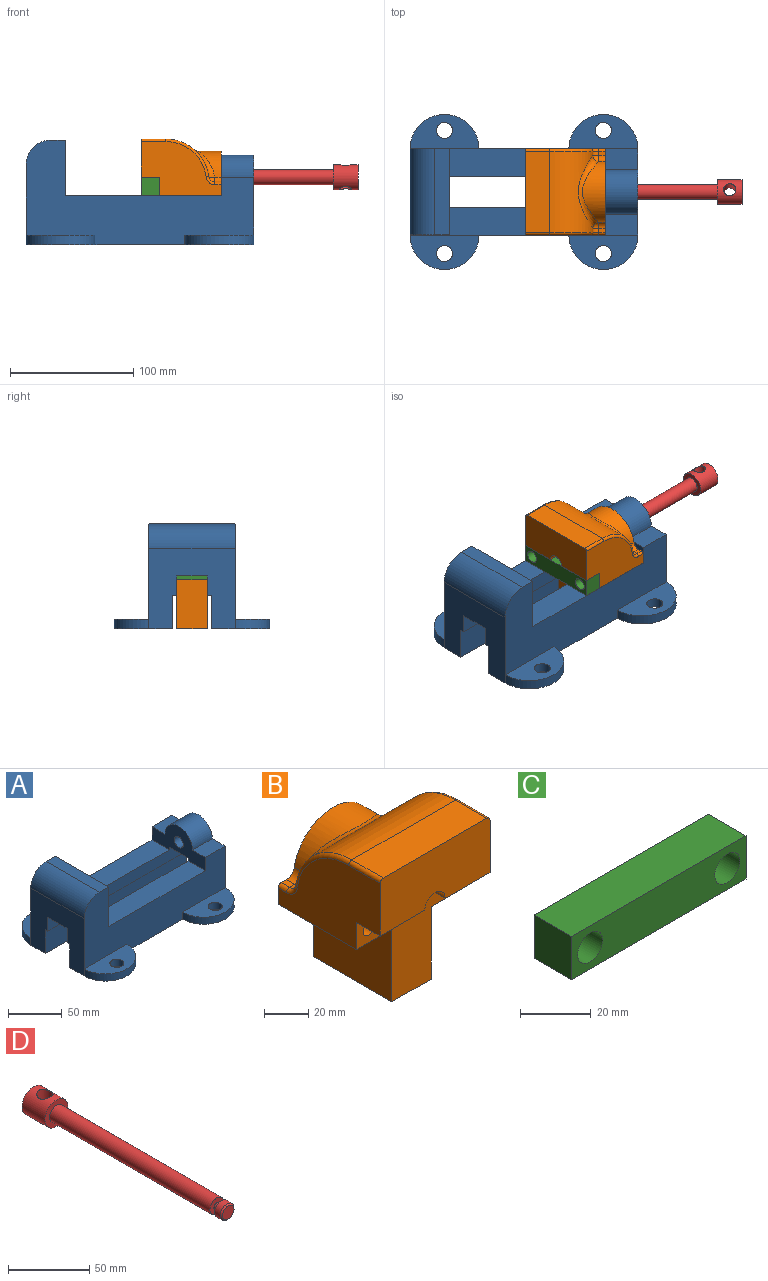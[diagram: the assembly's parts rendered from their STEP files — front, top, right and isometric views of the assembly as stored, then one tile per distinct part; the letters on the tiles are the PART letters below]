
ASSEMBLY  parts=4 mates=5
PART A: 36 faces, bbox 185x126x85 mm
  f0: plane 185x85mm, normal (0,1,0), area 8248.2mm2, adj f2,f3,f5,f6,f7,f8,f9,f10
  f1: plane 185x47mm, normal (0,0,-1), area 5712.5mm2, adj f2,f3,f11,f15,f30,f32,f33,f35
  f2: plane 73x70mm, normal (1,0,0), area 2981.8mm2, adj f0,f1,f9,f11,f12,f13,f14,f15
  f3: plane 70x65mm, normal (-1,0,0), area 3286mm2, adj f0,f1,f8,f9,f11,f15,f16,f17
  f4: plane 127x22.5mm, normal (0,0,1), area 2857.5mm2, adj f5,f6,f11,f22
  f5: plane 70x33mm, normal (-1,0,0), area 1370.8mm2, adj f0,f4,f10,f11,f12,f13,f14,f18
  f6: plane 70x45mm, normal (1,0,0), area 3075mm2, adj f0,f4,f7,f10,f11,f19,f21,f22
  f7: plane 70x12mm, normal (0,0,1), area 840mm2, adj f0,f6,f8,f11
  f8: cylinder r=20mm len=70mm, axis (0,1,0), area 2199.1mm2, adj f0,f3,f7,f11
  f9: plane 185x47mm, normal (0,0,-1), area 5712.5mm2, adj f0,f2,f3,f16,f25,f26,f28,f29
  f10: plane 127x22.5mm, normal (0,0,1), area 2857.5mm2, adj f0,f5,f6,f21
  f11: plane 185x85mm, normal (0,-1,0), area 8248.2mm2, adj f1,f2,f3,f4,f5,f6,f7,f8
  f12: cylinder r=18mm len=36mm, axis (1,0,0), area 1470.3mm2, adj f2,f5,f13,f14
  f13: plane 26x17mm, normal (0,0,1), area 442mm2, adj f2,f5,f11,f12
  f14: plane 26x17mm, normal (0,0,1), area 442mm2, adj f0,f2,f5,f12
  f15: plane 185x27mm, normal (0,1,0), area 4995mm2, adj f1,f2,f3,f20
  f16: plane 185x27mm, normal (0,-1,0), area 4995mm2, adj f2,f3,f9,f17
  f17: plane 185x3.5mm, normal (0,0,-1), area 647.5mm2, adj f2,f3,f16,f21
  f18: plane 26x25mm, normal (0,0,-1), area 650mm2, adj f2,f5,f21,f22
  f19: plane 32x25mm, normal (0,0,-1), area 800mm2, adj f3,f6,f21,f22
  f20: plane 185x3.5mm, normal (0,0,-1), area 647.5mm2, adj f2,f3,f15,f22
  f21: plane 185x16mm, normal (0,-1,0), area 2579mm2, adj f2,f3,f5,f6,f10,f17,f18,f19
  f22: plane 185x16mm, normal (0,1,0), area 2579mm2, adj f2,f3,f4,f5,f6,f18,f19,f20
  f23: cylinder r=6mm len=26mm, axis (1,0,0), area 980.2mm2, adj f2,f5
  f24: plane 56x28mm, normal (0,0,1), area 1098.8mm2, adj f0,f25,f26
  f25: cylinder r=28mm len=56mm, axis (0,0,-1), area 703.7mm2, adj f0,f2,f9,f24
  f26: cylinder r=6.5mm len=13mm, axis (0,0,-1), area 326.7mm2, adj f9,f24
  f27: plane 56x28mm, normal (0,0,1), area 1098.8mm2, adj f0,f28,f29
  f28: cylinder r=28mm len=56mm, axis (0,0,-1), area 703.7mm2, adj f0,f3,f9,f27
  f29: cylinder r=6.5mm len=13mm, axis (0,0,-1), area 326.7mm2, adj f9,f27
  f30: cylinder r=28mm len=56mm, axis (0,0,-1), area 703.7mm2, adj f1,f2,f11,f31
  f31: plane 56x28mm, normal (0,0,1), area 1098.8mm2, adj f11,f30,f32
  f32: cylinder r=6.5mm len=13mm, axis (0,0,-1), area 326.7mm2, adj f1,f31
  f33: cylinder r=28mm len=56mm, axis (0,0,-1), area 703.7mm2, adj f1,f3,f11,f34
  f34: plane 56x28mm, normal (0,0,1), area 1098.8mm2, adj f11,f33,f35
  f35: cylinder r=6.5mm len=13mm, axis (0,0,-1), area 326.7mm2, adj f1,f34
PART B: 35 faces, bbox 70x65x88.9 mm
  f0: plane 28.5x15mm, normal (0,0,-1), area 427.5mm2, adj f6,f7,f9,f17
  f1: plane 28.5x15mm, normal (0,0,-1), area 427.5mm2, adj f6,f8,f9,f17
  f2: plane 5.31x3.42mm, normal (0,0,1), area 18.2mm2, adj f5,f20,f21,f34
  f3: cylinder r=35mm len=66mm, axis (-1,0,0), area 2250.4mm2, adj f11,f21,f22,f26,f28,f32
  f4: plane 50x25mm, normal (0,0,-1), area 1250mm2, adj f5,f6,f12,f14
  f5: plane 76x70mm, normal (0,1,0), area 2557mm2, adj f2,f4,f7,f8,f10,f12,f13,f14
  f6: plane 70x55mm, normal (0,-1,0), area 1915.2mm2, adj f0,f1,f4,f7,f8,f12,f13,f14
  f7: plane 65x44mm, normal (1,0,0), area 1990.2mm2, adj f0,f5,f6,f9,f15,f31,f32,f33
  f8: plane 65x44mm, normal (-1,0,0), area 1990.2mm2, adj f1,f5,f6,f9,f13,f27,f28,f29
  f9: plane 70x31mm, normal (0,-1,0), area 2101.9mm2, adj f0,f1,f7,f8,f11,f17,f27,f31
  f10: plane 5.31x3.42mm, normal (0,0,1), area 18.2mm2, adj f5,f22,f23,f30
  f11: plane 66x20mm, normal (0,0,1), area 1320mm2, adj f3,f9,f27,f31
  f12: plane 50x40mm, normal (-1,0,0), area 2000mm2, adj f4,f5,f6,f13
  f13: plane 50x22.5mm, normal (0,0,-1), area 1125mm2, adj f5,f6,f8,f12
  f14: plane 50x40mm, normal (1,0,0), area 2000mm2, adj f4,f5,f6,f15
  f15: plane 50x22.5mm, normal (0,0,-1), area 1125mm2, adj f5,f6,f7,f14
  f16: cylinder r=25mm len=49.3mm, axis (0,1,0), area 854.7mm2, adj f5,f20,f23,f26
  f17: cylinder r=6.5mm len=65mm, axis (0,1,0), area 2348.3mm2, adj f0,f1,f5,f6,f9
  f18: cylinder r=3.3mm len=50mm, axis (0,1,0), area 1036.7mm2, adj f5,f6
  f19: cylinder r=3.3mm len=50mm, axis (0,1,0), area 1036.7mm2, adj f5,f6
  f20: cylinder r=5mm len=5.31mm, axis (0,1,0), area 37.3mm2, adj f2,f5,f16,f24
  f21: cylinder r=5mm len=4.96mm, axis (-1,0,0), area 24.7mm2, adj f2,f3,f24,f33
  f22: cylinder r=5mm len=4.96mm, axis (-1,0,0), area 24.7mm2, adj f3,f10,f25,f29
  f23: cylinder r=5mm len=5.31mm, axis (0,1,0), area 37.3mm2, adj f5,f10,f16,f25
  f24: sphere r=5mm, area 32mm2, adj f20,f21,f26
  f25: sphere r=5mm, area 32mm2, adj f22,f23,f26
  f26: bspline ~59.69x24.08mm, area 433.7mm2, adj f3,f16,f24,f25
  f27: cylinder r=2mm len=20mm, axis (0,-1,0), area 62.8mm2, adj f8,f9,f11,f28
  f28: torus R=33mm, axis (1,0,0), area 155.6mm2, adj f3,f8,f27,f29
  f29: torus R=7mm, axis (1,0,0), area 26mm2, adj f8,f22,f28,f30
  f30: cylinder r=2mm len=5.31mm, axis (0,-1,0), area 16.7mm2, adj f5,f8,f10,f29
  f31: cylinder r=2mm len=20mm, axis (0,1,0), area 62.8mm2, adj f7,f9,f11,f32
  f32: torus R=33mm, axis (1,0,0), area 155.6mm2, adj f3,f7,f31,f33
  f33: torus R=7mm, axis (1,0,0), area 26mm2, adj f7,f21,f32,f34
  f34: cylinder r=2mm len=5.31mm, axis (0,1,0), area 16.7mm2, adj f2,f5,f7,f33
PART C: 16 faces, bbox 70x15x15 mm
  f0: plane 70x15mm, normal (0,1,0), area 958.9mm2, adj f1,f3,f4,f5,f6,f9,f12
  f1: plane 70x15mm, normal (0,0,1), area 1050mm2, adj f0,f2,f4,f5
  f2: plane 70x15mm, normal (0,-1,0), area 892.9mm2, adj f1,f3,f4,f5,f8,f11
  f3: plane 70x15mm, normal (0,0,-1), area 960mm2, adj f0,f2,f4,f5,f12,f13,f14,f15
  f4: plane 15x15mm, normal (1,0,0), area 225mm2, adj f0,f1,f2,f3
  f5: plane 15x15mm, normal (-1,0,0), area 225mm2, adj f0,f1,f2,f3
  f6: cylinder r=3.5mm len=7mm, axis (0,-1,0), area 110mm2, adj f0,f7
  f7: plane 10x10mm, normal (0,-1,0), area 40.1mm2, adj f6,f8
  f8: cylinder r=5mm len=10mm, axis (0,-1,0), area 314.2mm2, adj f2,f7
  f9: cylinder r=3.5mm len=7mm, axis (0,-1,0), area 110mm2, adj f0,f10
  f10: plane 10x10mm, normal (0,-1,0), area 40.1mm2, adj f9,f11
  f11: cylinder r=5mm len=10mm, axis (0,-1,0), area 314.2mm2, adj f2,f10
  f12: cylinder r=3mm len=6mm, axis (0,-1,0), area 28.3mm2, adj f0,f3,f13
  f13: plane 12x6mm, normal (0,-1,0), area 42.4mm2, adj f3,f12,f14
  f14: cylinder r=6mm len=12mm, axis (0,-1,0), area 113.1mm2, adj f3,f13,f15
  f15: plane 12x6mm, normal (0,1,0), area 56.5mm2, adj f3,f14
PART D: 11 faces, bbox 20x170x20 mm
  f0: plane 20x20mm, normal (0,1,0), area 314.2mm2, adj f1
  f1: cylinder r=10mm len=20mm, axis (0,1,0), area 1094.4mm2, adj f0,f2,f10
  f2: plane 20x20mm, normal (0,-1,0), area 201.1mm2, adj f1,f3
  f3: cylinder r=6mm len=140mm, axis (0,1,0), area 5277.9mm2, adj f2,f4
  f4: plane 12x12mm, normal (0,-1,0), area 93.5mm2, adj f3,f5
  f5: cylinder r=2.5mm len=5mm, axis (0,1,0), area 62.8mm2, adj f4,f6
  f6: plane 12x12mm, normal (0,1,0), area 93.5mm2, adj f5,f7
  f7: cylinder r=6mm len=12mm, axis (0,1,0), area 188.5mm2, adj f6,f9
  f8: plane 10x10mm, normal (0,-1,0), area 78.5mm2, adj f9
  f9: cone r=6mm half-angle=45deg, axis (0,1,0), area 48.9mm2, adj f7,f8
  f10: cylinder r=5mm len=20mm, axis (0,0,1), area 587mm2, adj f1
PLACE A t=(76.5,0,-0.5)mm
PLACE B rot(axis=(0,0,-1),90deg) t=(111.37,0,-10.58)mm
PLACE C rot(axis=(-0.71,-0.71,0),180deg) t=(85,0,4.5)mm
PLACE D rot(axis=(0.71,0.71,-0.07),172.4deg) t=(124.59,0,12)mm
MATE cylindrical D.f1 <-> A.f23  axis (1,0,0) through (163.5,0,12)mm
MATE planar B.f14 <-> A.f22  axis (0,-1,0) through (117.5,-12.5,-23)mm
MATE revolute C.f12 <-> D.f1  axis (1,0,0) through (83.5,0,12)mm
MATE planar B.f15 <-> A.f4  axis (0,0,-1) through (117.5,-23.75,-3)mm
MATE fastened B.f1 <-> C.f3  axis (0,0,-1) through (85,35,12)mm
